# Revit family: ROSENBERG_Z
name_source: partatom
category: Wyposażenie mechaniczne
revit_build: Autodesk Revit 2017 (Build: 20160225_1515(x64)
units: mm (PartAtom-declared; Revit-internal decimal feet)

## family parameters
Numer OmniClass = 23.75.00.00
Oparty na płaszczyźnie roboczej = Nie
Punkt obliczania pomieszczeń = Nie
Tnij formami wycięć po wczytaniu = Nie
Typ części = Dzieli na
Tytuł OmniClass = Climate Control (HVAC)
Współdzielony = Tak
Wymiar okrągłego złącza = Użyj średnicy
Zawsze pionowo = Tak

## types (10) — shared parameters
Date = 10.2018
Frequency = 50 Hz
Material = <Wg kategorii>
Opis = Tube Fan
Producent = Rosenberg
URL = https://www.rosenberg.pl
Version = 1
Voltage = 230 V

## per-type parameters (varying)
| type | Air_flow | Current | Diamater_connector | Diameter_hole | Height | Lenght_box | Length | Power | Pressure | Protection Class | Weight | Width | X_connector | Y_connector | param_b1 | param_f1 |
| 250.3EF R1 | 639.0 m³/h | 1 A | 250 mm  [stored 0.82021 ft] | 244 mm | 354 mm | 420 mm | 520 mm | 200 W | 408.0 Pa | IP44 | 17.50 kg | 465 mm | 233 mm | 180 mm | 130 mm | 347 mm |
| 200.3DF R1 | 446.0 m³/h | 1 A | 200 mm  [stored 0.656168 ft] | 194 mm | 314 mm | 390 mm | 490 mm | 124 W | 288.0 Pa | IP44 | 17.50 kg | 420 mm | 210 mm | 150 mm | 123 mm | 327 mm |
| 160.3CF R1 | 296.0 m³/h | 0 A | 160 mm | 154 mm | 264 mm | 360 mm  [stored 1.1811 ft] | 460 mm | 100 W | 238.0 Pa | IP44 | 14.50 kg | 380 mm | 190 mm | 125 mm | 115 mm | 307 mm |
| 125.2CA R1 | 0.0 m³/h | 0 A | 125 mm | 119 mm | 244 mm | 360 mm  [stored 1.1811 ft] | 460 mm | 29 W | 0.0 Pa | IP44 | 13.00 kg | 380 mm | 190 mm | 105 mm | 115 mm | 307 mm |
| 400.5FA R1 | 1545.0 m³/h | 1 A | 400 mm | 394 mm | 470 mm | 650 mm | 750 mm | 290 W | 245.0 Pa | IP44 | 28.00 kg | 645 mm | 323 mm | 242 mm  [stored 0.793963 ft] | 188 mm | 500 mm |
| 355.5FA E1 | 1059.0 m³/h | 3 A | 355 mm | 349 mm | 420 mm | 580 mm | 680 mm | 600 W | 337.0 Pa | IP54 | 44.00 kg | 620 mm | 230 mm | 228 mm | 170 mm | 453 mm |
| 315.4EC R1 | 911.0 m³/h | 1 A | 315 mm  [stored 1.03346 ft] | 309 mm  [stored 1.01378 ft] | 420 mm | 580 mm | 680 mm | 143 W | 177.0 Pa | IP44 | 21.00 kg | 595 mm | 298 mm | 208 mm | 170 mm | 453 mm |
| 160.3CA R2 | 266.0 m³/h | 0 A | 160 mm | 154 mm | 264 mm | 360 mm  [stored 1.1811 ft] | 460 mm | 60 W | 197.0 Pa | IP44 | 14.00 kg | 380 mm | 190 mm | 125 mm | 115 mm | 307 mm |
| 315.5FA E1 | 1024.0 m³/h | 3 A | 315 mm  [stored 1.03346 ft] | 309 mm  [stored 1.01378 ft] | 420 mm | 580 mm | 680 mm | 550 W | 326.0 Pa | IP54 | 44.00 kg | 595 mm | 298 mm | 208 mm | 170 mm | 453 mm |
| 355.5FA R1 | 1217.0 m³/h | 1 A | 355 mm | 349 mm | 460 mm | 600 mm | 700 mm | 290 W | 272.0 Pa | IP44 | 26.00 kg | 620 mm | 310 mm | 230 mm | 175 mm | 467 mm |

note: column(s) folded — value = type name in every type: Model

note: [stored X ft] marks values corroborated as IEEE doubles in the binary element streams (Revit-internal decimal feet)

## geometry (parser evidence)
native form markers: Blend x4, Sweep x5
no freeform markers — native parametric forms only
